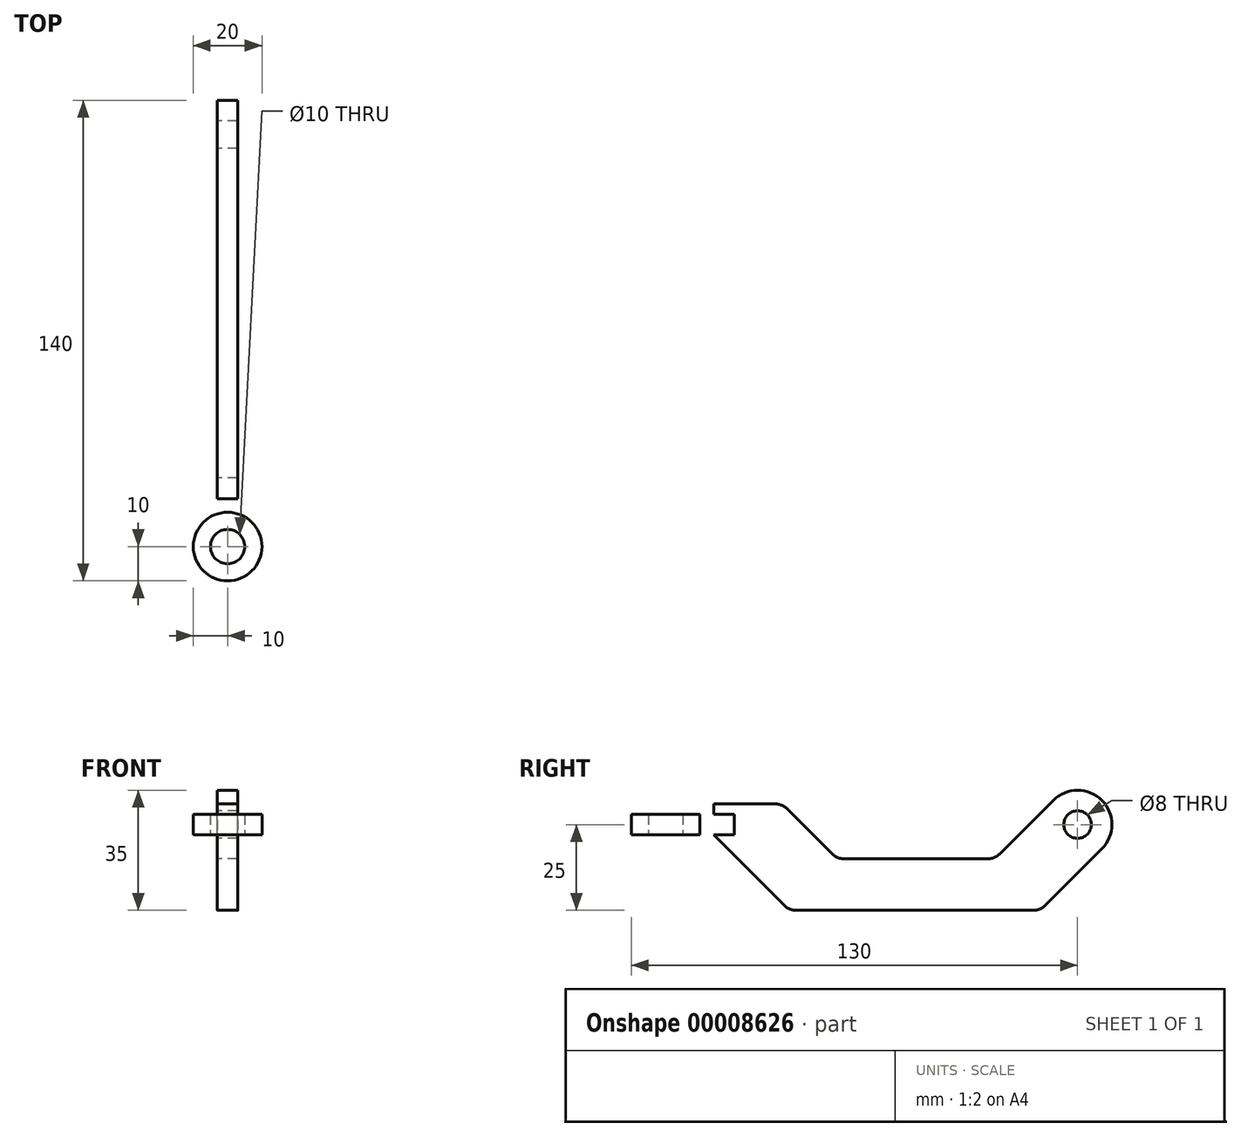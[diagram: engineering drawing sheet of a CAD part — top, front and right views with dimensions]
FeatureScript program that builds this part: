
annotation { "Feature Type Name" : "Feature", "Feature Type Description" : "" }
export const myFeature = defineFeature(function(context is Context, id is Id, definition is map)
    precondition{}
    {
        {
            var Q0;
            Q0=qCreatedBy(makeId("Right.planeOp"),FACE);
            var sketch = newSketch(context, id + "F0", { "sketchPlane" : qUnion([Q0])});
            skCircle(sketch, "E0", {"center": v(0, 0) * mm, "radius": 4 * mm});
            skLineSegment(sketch, "E1", {"start": v(-120, 18.19) * mm, "end": v(-120, -19.63) * mm, "construction": true});
            skCircle(sketch, "E2", {"center": v(0, 0) * mm, "radius": 10 * mm});
            skLineSegment(sketch, "E3", {"start": v(46.57, -10) * mm, "end": v(-137.44, -10) * mm, "construction": true});
            skLineSegment(sketch, "E4", {"start": v(-7.07, 7.07) * mm, "end": v(-24.14, -10) * mm});
            skLineSegment(sketch, "E5", {"start": v(-84, -25) * mm, "end": v(-10.86, -25) * mm});
            skLineSegment(sketch, "E6", {"start": v(-10.86, -25) * mm, "end": v(7.07, -7.07) * mm});
            skLineSegment(sketch, "E7", {"start": v(-24.14, -10) * mm, "end": v(-70, -10) * mm});
            skLineSegment(sketch, "E8", {"start": v(-70, -10) * mm, "end": v(-86, 6) * mm});
            skLineSegment(sketch, "E9", {"start": v(-86, 6) * mm, "end": v(-106, 6) * mm});
            skLineSegment(sketch, "E10", {"start": v(-106, -3) * mm, "end": v(-84, -25) * mm});
            skLineSegment(sketch, "E11", {"start": v(-106, -3) * mm, "end": v(-100, -3) * mm});
            skLineSegment(sketch, "E12", {"start": v(-100, -3) * mm, "end": v(-100, 3) * mm});
            skLineSegment(sketch, "E13", {"start": v(-100, 3) * mm, "end": v(-106, 3) * mm});
            skLineSegment(sketch, "E14", {"start": v(-106, 3) * mm, "end": v(-106, 6) * mm});
            skLineSegment(sketch, "E15", {"start": v(-106, 3) * mm, "end": v(-106, -3) * mm, "construction": true});
            skSolve(sketch);
        }
        {
            var Q0;
            {var subQ1=sQuery(id+"F0.wireOp",EDGE,"E4");Q0=makeQuery(id+"F0.imprint","IMPRINT",FACE,{"disambiguationData":[TD([[makeQuery(id+"F0.imprint","IMPRINT",EDGE,{"derivedFrom":subQ1}),1.0]])]});}
            var Q1;
            Q1=makeQuery(id+"F0.imprint","IMPRINT",FACE,{"disambiguationData":[TD([[makeQuery(id+"F0.imprint","IMPRINT",EDGE,{"derivedFrom":sQuery(id+"F0.wireOp",EDGE,"E0")}),-1.0]])]});
            extrude(context, id + "F1", {"entities" : qUnion([Q0, Q1]), "depth" : 3 * mm, "hasSecondDirection" : true, "secondDirectionOppositeDirection" : true, "secondDirectionDepth" : 3 * mm});
        }
        {
            var Q0;
            Q0=qCreatedBy(makeId("Top.planeOp"),FACE);
            var sketch = newSketch(context, id + "F2", { "sketchPlane" : qUnion([Q0])});
            skLineSegment(sketch, "E16.1.1", {"start": v(-3, -100) * mm, "end": v(3, -100) * mm});
            skLineSegment(sketch, "E16.1.3", {"start": v(3, -100) * mm, "end": v(-3, -100) * mm});
            skPoint(sketch, "E17.0", {"position": v(0, -120) * mm});
            skCircle(sketch, "E18", {"center": v(0, -120) * mm, "radius": 10 * mm});
            skCircle(sketch, "E19", {"center": v(0, -120) * mm, "radius": 5 * mm});
            skLineSegment(sketch, "E20", {"start": v(-10, -120) * mm, "end": v(-10, -85) * mm});
            skLineSegment(sketch, "E21", {"start": v(-10, -85) * mm, "end": v(-3, -85) * mm});
            skLineSegment(sketch, "E22", {"start": v(-3, -85) * mm, "end": v(-3, -100) * mm});
            skLineSegment(sketch, "E23.0.MirrorCS", {"start": v(3, -85) * mm, "end": v(3, -100) * mm});
            skLineSegment(sketch, "E24.0.MirrorCS", {"start": v(10, -85) * mm, "end": v(3, -85) * mm});
            skLineSegment(sketch, "E25.0.MirrorCS", {"start": v(10, -120) * mm, "end": v(10, -85) * mm});
            skSolve(sketch);
        }
        {
            var Q0;
            Q0=makeQuery(id+"F2.imprint","IMPRINT",FACE,{"disambiguationData":[TD([[makeQuery(id+"F2.imprint","IMPRINT",EDGE,{"derivedFrom":sQuery(id+"F2.wireOp",EDGE,"E16.1.3")}),1.0]])]});
            var Q1;
            Q1=makeQuery(id+"F2.imprint","IMPRINT",FACE,{"disambiguationData":[TD([[makeQuery(id+"F2.imprint","IMPRINT",EDGE,{"derivedFrom":sQuery(id+"F2.wireOp",EDGE,"E19")}),-1.0]])]});
            extrude(context, id + "F3", {"entities" : qUnion([Q0, Q1]), "depth" : 3 * mm, "hasSecondDirection" : true, "secondDirectionOppositeDirection" : true, "secondDirectionDepth" : 3 * mm});
        }
        {
            var Q0;
            Q0=makeQuery(id+"F1.opExtrude","SWEPT_EDGE",EDGE,{"disambiguationData":[OSD([sQuery(id+"F0.wireOp",EDGE,"E8"),sQuery(id+"F0.wireOp",EDGE,"E9")])]});
            var Q1;
            Q1=makeQuery(id+"F1.opExtrude","SWEPT_EDGE",EDGE,{"disambiguationData":[OSD([sQuery(id+"F0.wireOp",EDGE,"E7"),sQuery(id+"F0.wireOp",EDGE,"E8")])]});
            var Q2;
            Q2=makeQuery(id+"F1.opExtrude","SWEPT_EDGE",EDGE,{"disambiguationData":[OSD([sQuery(id+"F0.wireOp",EDGE,"E4"),sQuery(id+"F0.wireOp",EDGE,"E7")])]});
            var Q3;
            Q3=makeQuery(id+"F1.opExtrude","SWEPT_EDGE",EDGE,{"disambiguationData":[OSD([sQuery(id+"F0.wireOp",EDGE,"E5"),sQuery(id+"F0.wireOp",EDGE,"E10")])]});
            var Q4;
            Q4=makeQuery(id+"F1.opExtrude","SWEPT_EDGE",EDGE,{"disambiguationData":[OSD([sQuery(id+"F0.wireOp",EDGE,"E5"),sQuery(id+"F0.wireOp",EDGE,"E6")])]});
            fillet(context, id + "F4", {"entities" : qUnion([Q0, Q1, Q2, Q3, Q4]), "radius" : 5 * mm, "tangentPropagation" : true, "allowEdgeOverflow" : false});
        }
    });
